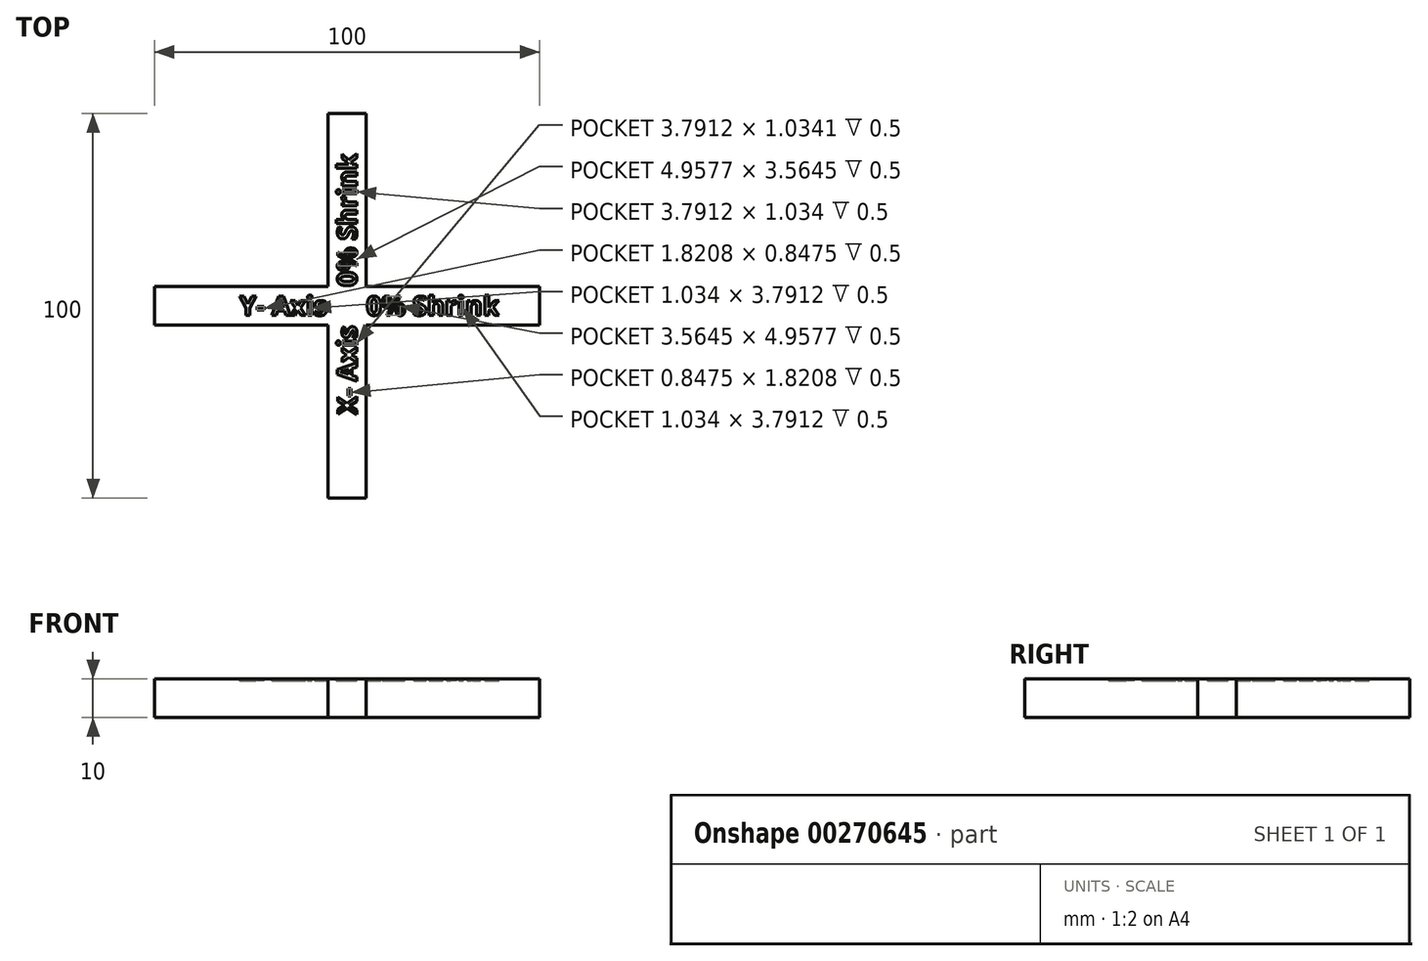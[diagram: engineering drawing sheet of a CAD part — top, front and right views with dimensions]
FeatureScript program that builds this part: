
annotation { "Feature Type Name" : "Feature", "Feature Type Description" : "" }
export const myFeature = defineFeature(function(context is Context, id is Id, definition is map)
    precondition{}
    {
        {
            var Q0;
            Q0=qCreatedBy(makeId("Top.planeOp"),FACE);
            var sketch = newSketch(context, id + "F0", { "sketchPlane" : qUnion([Q0])});
            skLineSegment(sketch, "E0.bottom", {"start": v(50, -5) * mm, "end": v(-50, -5) * mm});
            skLineSegment(sketch, "E0.top", {"start": v(50, 5) * mm, "end": v(-50, 5) * mm});
            skLineSegment(sketch, "E0.left", {"start": v(50, -5) * mm, "end": v(50, 5) * mm});
            skLineSegment(sketch, "E0.right", {"start": v(-50, -5) * mm, "end": v(-50, 5) * mm});
            skPoint(sketch, "E0.middle", {"position": v(0, 0) * mm});
            skLineSegment(sketch, "E1.bottom", {"start": v(-5, 50) * mm, "end": v(5, 50) * mm});
            skLineSegment(sketch, "E1.top", {"start": v(-5, -50) * mm, "end": v(5, -50) * mm});
            skLineSegment(sketch, "E1.left", {"start": v(-5, 50) * mm, "end": v(-5, -50) * mm});
            skLineSegment(sketch, "E1.right", {"start": v(5, 50) * mm, "end": v(5, -50) * mm});
            skSolve(sketch);
        }
        {
            var Q0;
            {var subQ0=sQuery(id+"F0.wireOp",EDGE,"E0.right");Q0=makeQuery(id+"F0.imprint","IMPRINT",FACE,{"disambiguationData":[TD([[makeQuery(id+"F0.imprint","IMPRINT",EDGE,{"derivedFrom":subQ0}),-1.0]])]});}
            var Q1;
            {var subQ5=sQuery(id+"F0.wireOp",EDGE,"E1.bottom");Q1=makeQuery(id+"F0.imprint","IMPRINT",FACE,{"disambiguationData":[TD([[makeQuery(id+"F0.imprint","IMPRINT",EDGE,{"derivedFrom":subQ5}),-1.0]])]});}
            var Q2;
            {var subQ0=sQuery(id+"F0.wireOp",EDGE,"E1.right");var subQ1=sQuery(id+"F0.wireOp",EDGE,"E0.bottom");var subQ2=makeQuery(id+"F0.imprint","INTERSECT",VERTEX,{"derivedFrom":[subQ1,subQ0]});Q2=makeQuery(id+"F0.imprint","IMPRINT",FACE,{"disambiguationData":[TD([[makeQuery(id+"F0.imprint","IMPRINT",EDGE,{"disambiguationData":[TD([[subQ2,-1.0]])],"derivedFrom":subQ1}),-1.0]])]});}
            var Q3;
            {var subQ0=sQuery(id+"F0.wireOp",EDGE,"E0.left");Q3=makeQuery(id+"F0.imprint","IMPRINT",FACE,{"disambiguationData":[TD([[makeQuery(id+"F0.imprint","IMPRINT",EDGE,{"derivedFrom":subQ0}),1.0]])]});}
            var Q4;
            {var subQ5=sQuery(id+"F0.wireOp",EDGE,"E1.top");Q4=makeQuery(id+"F0.imprint","IMPRINT",FACE,{"disambiguationData":[TD([[makeQuery(id+"F0.imprint","IMPRINT",EDGE,{"derivedFrom":subQ5}),1.0]])]});}
            extrude(context, id + "F1", {"entities" : qUnion([Q0, Q1, Q2, Q3, Q4]), "depth" : 10 * mm});
        }
        {
            var Q0;
            Q0=makeQuery(id+"F1.opExtrude","CAP_FACE",FACE,{"disambiguationData":[OSD([sQuery(id+"F0.wireOp",EDGE,"E0.bottom"),sQuery(id+"F0.wireOp",EDGE,"E0.top"),sQuery(id+"F0.wireOp",EDGE,"E0.left"),sQuery(id+"F0.wireOp",EDGE,"E0.right"),sQuery(id+"F0.wireOp",EDGE,"E1.bottom"),sQuery(id+"F0.wireOp",EDGE,"E1.top"),sQuery(id+"F0.wireOp",EDGE,"E1.left"),sQuery(id+"F0.wireOp",EDGE,"E1.right")])],"isStart":false});
            var sketch = newSketch(context, id + "F2", { "sketchPlane" : qUnion([Q0])});
            skText(sketch, "E2", { "text": "Y- Axis", "fontName": "OpenSans-Bold.ttf"});
            skPoint(sketch, "E3", {"position": v(-27.94, 0) * mm});
            skText(sketch, "E4", { "text": "0% Shrink", "fontName": "OpenSans-Bold.ttf"});
            skPoint(sketch, "E5", {"position": v(40, 0) * mm});
            skText(sketch, "E6", { "text": "X- Axis", "fontName": "OpenSans-Bold.ttf"});
            skPoint(sketch, "E7", {"position": v(0, -5) * mm});
            skText(sketch, "E8", { "text": "0% Shrink", "fontName": "OpenSans-Bold.ttf"});
            skPoint(sketch, "E9", {"position": v(0, 22.5) * mm});
            const initialGuessF2  = {"E2": [-0.02794, -0.0025, 1, 0, 0.005], "E4": [0.005, -0.0025, 1, 0, 0.005], "E6": [0.0025, -0.02823, 0, 1, 0.005], "E8": [0.0025, 0.005, 0, 1, 0.005]};
            skSetInitialGuess(sketch, initialGuessF2);
            skSolve(sketch);
        }
        {
            var Q0;
            Q0 = qSketchRegion(id + "F2", true);
            extrude(context, id + "F3", {"entities" : qUnion([Q0]), "operationType" : NewBodyOperationType.REMOVE, "oppositeDirection" : true, "depth" : .5 * mm});
        }
    });
